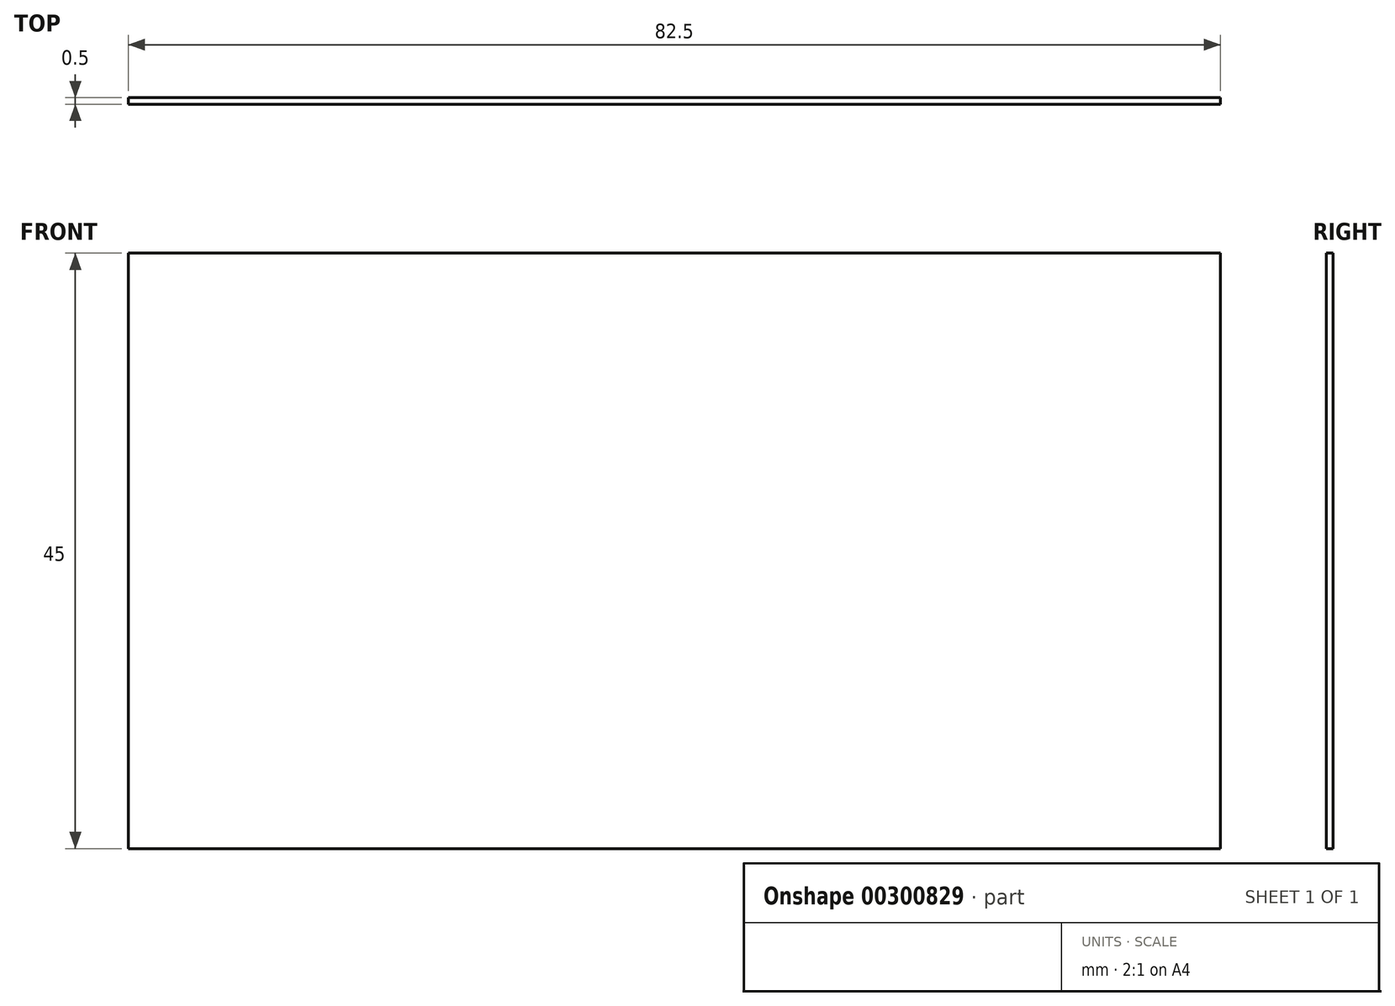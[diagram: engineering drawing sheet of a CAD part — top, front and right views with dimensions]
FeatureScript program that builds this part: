
annotation { "Feature Type Name" : "Feature", "Feature Type Description" : "" }
export const myFeature = defineFeature(function(context is Context, id is Id, definition is map)
    precondition{}
    {
        {
            var Q0;
            Q0=qCreatedBy(makeId("Front.planeOp"),FACE);
            var sketch = newSketch(context, id + "F0", { "sketchPlane" : qUnion([Q0])});
            skLineSegment(sketch, "E0.bottom", {"start": v(0, 0) * mm, "end": v(1650, 0) * mm});
            skLineSegment(sketch, "E0.top", {"start": v(0, -900) * mm, "end": v(1650, -900) * mm});
            skLineSegment(sketch, "E0.left", {"start": v(0, 0) * mm, "end": v(0, -900) * mm});
            skLineSegment(sketch, "E0.right", {"start": v(1650, 0) * mm, "end": v(1650, -900) * mm});
            skSolve(sketch);
        }
        {
            var Q0;
            Q0=makeQuery(id+"F0.imprint","IMPRINT",FACE,{"disambiguationData":[TD([[makeQuery(id+"F0.imprint","IMPRINT",EDGE,{"derivedFrom":sQuery(id+"F0.wireOp",EDGE,"E0.bottom")}),-1.0]])]});
            extrude(context, id + "F1", {"entities" : qUnion([Q0]), "depth" : 10 * mm});
        }
        {
            var Q0;
            Q0=makeQuery(id+"F1.opExtrude","SWEPT_BODY",BODY,{"disambiguationData":[OSD([sQuery(id+"F0.wireOp",EDGE,"E0.bottom"),sQuery(id+"F0.wireOp",EDGE,"E0.top"),sQuery(id+"F0.wireOp",EDGE,"E0.left"),sQuery(id+"F0.wireOp",EDGE,"E0.right")])]});
            var Q1;
            Q1=qCreatedBy(makeId("Origin.pointOp"),VERTEX);
            transform(context, id + "F2", {"entities" : qUnion([Q0]), "transformType" : TransformType.SCALE_UNIFORMLY, "scale" : 0.05, "scalePoint" : qUnion([Q1]), "makeCopy" : false});
        }
    });
